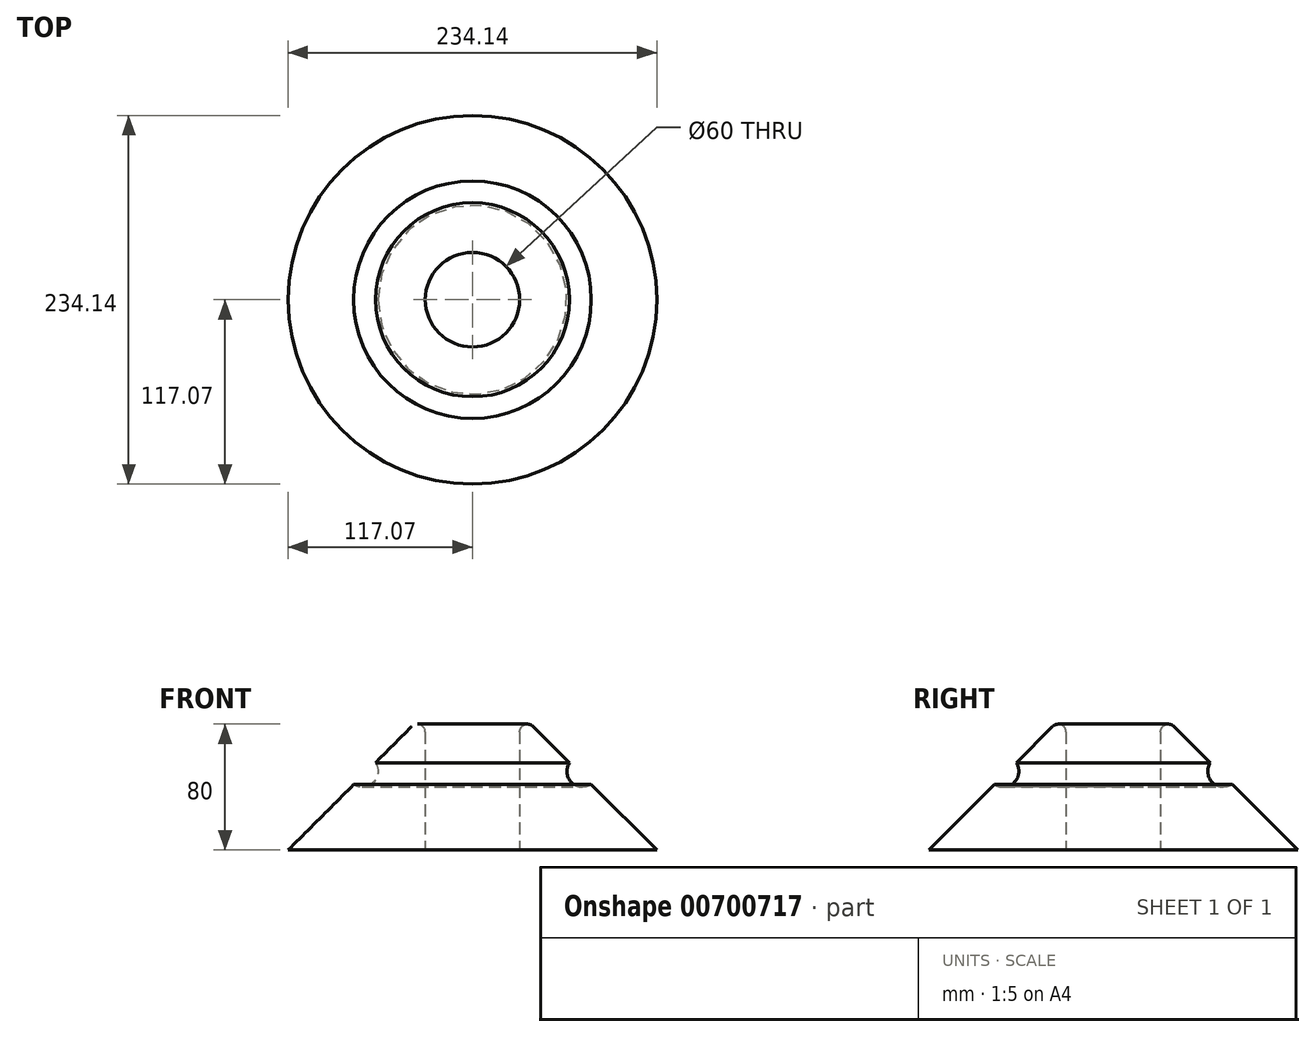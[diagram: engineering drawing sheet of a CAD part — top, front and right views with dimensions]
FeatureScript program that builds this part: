
annotation { "Feature Type Name" : "Feature", "Feature Type Description" : "" }
export const myFeature = defineFeature(function(context is Context, id is Id, definition is map)
    precondition{}
    {
        {
            var Q0;
            Q0=qCreatedBy(makeId("Front.planeOp"),FACE);
            var sketch = newSketch(context, id + "F0", { "sketchPlane" : qUnion([Q0])});
            skLineSegment(sketch, "E0", {"start": v(-30, 0) * mm, "end": v(-30, 75) * mm});
            skLineSegment(sketch, "E1", {"start": v(-38.54, 78.54) * mm, "end": v(-117.07, 0) * mm});
            skLineSegment(sketch, "E2", {"start": v(-117.07, 0) * mm, "end": v(-30, 0) * mm});
            skPoint(sketch, "E3.visualSharp", {"position": v(-30, 87.07) * mm});
            skArc(sketch, "E3.filletArc", {"start": v(-30, 75) * mm, "mid": v(-33.09, 79.62) * mm, "end": v(-38.54, 78.54) * mm});
            skLineSegment(sketch, "E4", {"start": v(0, 0) * mm, "end": v(0, 99.99) * mm, "construction": true});
            skSolve(sketch);
        }
        {
            var Q0;
            Q0=qCreatedBy(makeId("Front.planeOp"),FACE);
            var sketch = newSketch(context, id + "F1", { "sketchPlane" : qUnion([Q0])});
            skCircle(sketch, "E5", {"center": v(-70, 50) * mm, "radius": 10 * mm});
            skLineSegment(sketch, "E6", {"start": v(0, 0) * mm, "end": v(0, 100.24) * mm});
            skSolve(sketch);
        }
        {
            var Q0;
            Q0 = qSketchRegion(id + "F0", true);
            var Q1;
            Q1=sQuery(id+"F1.wireOp",EDGE,"E6");
            revolve(context, id + "F2", {"entities" : qUnion([Q0]), "axis" : qUnion([Q1]), "revolveType" : RevolveType.FULL});
        }
        {
            var Q0;
            Q0 = qSketchRegion(id + "F1", true);
            var Q1;
            Q1=sQuery(id+"F0.wireOp",EDGE,"E4");
            revolve(context, id + "F3", {"operationType" : NewBodyOperationType.REMOVE, "entities" : qUnion([Q0]), "axis" : qUnion([Q1]), "revolveType" : RevolveType.FULL, "oppositeDirection" : true});
        }
    });
